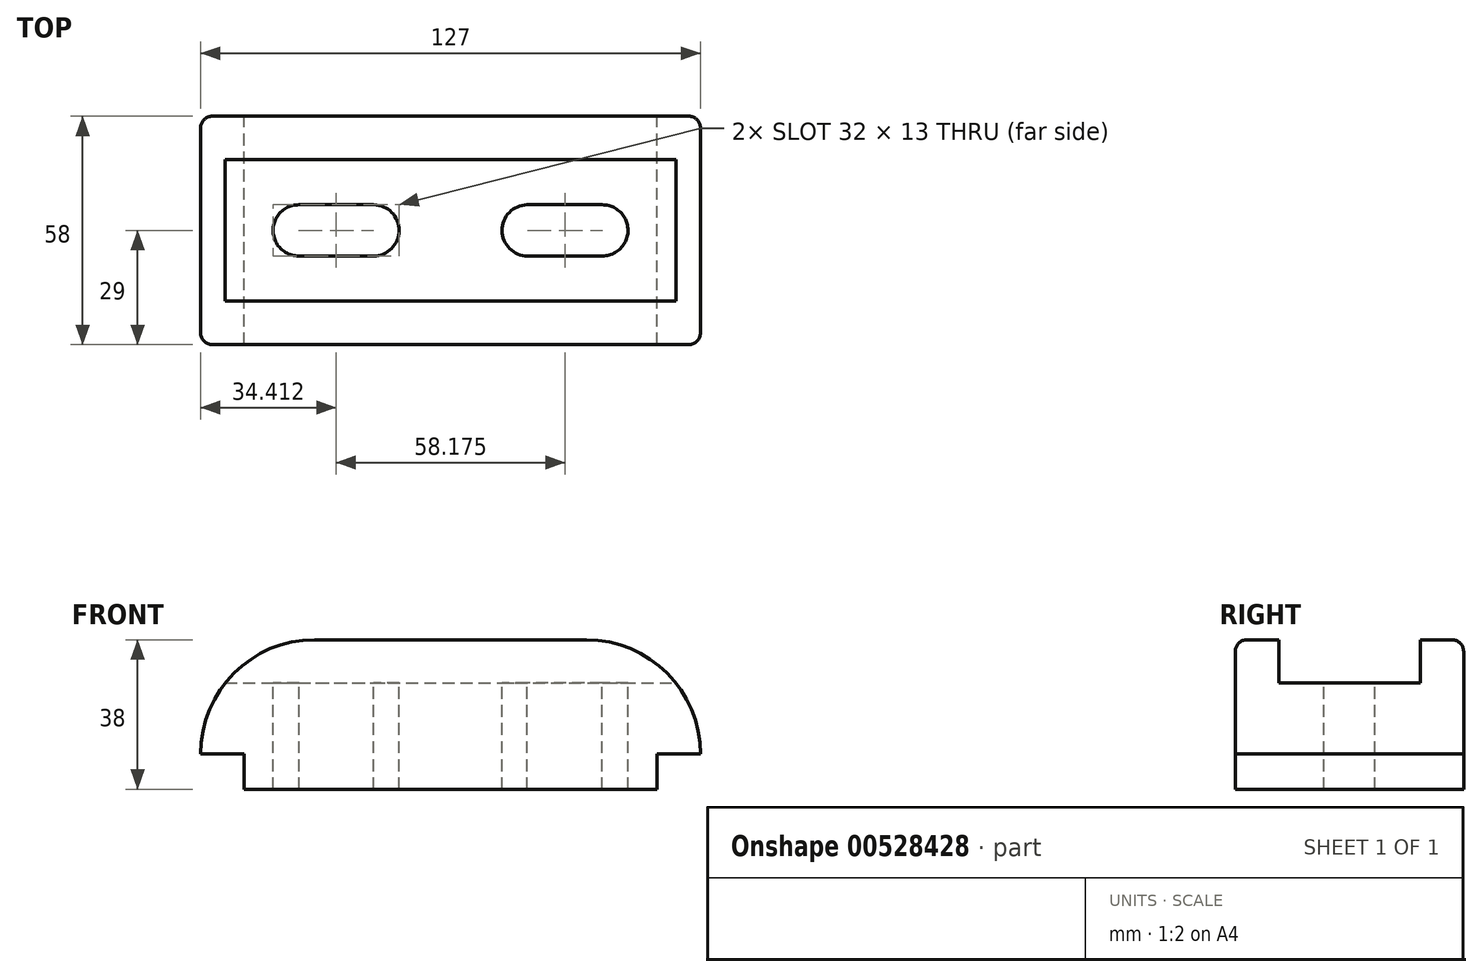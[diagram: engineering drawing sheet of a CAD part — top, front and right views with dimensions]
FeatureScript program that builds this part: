
annotation { "Feature Type Name" : "Feature", "Feature Type Description" : "" }
export const myFeature = defineFeature(function(context is Context, id is Id, definition is map)
    precondition{}
    {
        {
            var Q0;
            Q0=qCreatedBy(makeId("Front.planeOp"),FACE);
            var sketch = newSketch(context, id + "F0", { "sketchPlane" : qUnion([Q0])});
            skLineSegment(sketch, "E0.bottom", {"start": v(-34.5, 19) * mm, "end": v(34.5, 19) * mm});
            skLineSegment(sketch, "E0.top", {"start": v(-52.5, -19) * mm, "end": v(52.5, -19) * mm});
            skLineSegment(sketch, "E0.left", {"start": v(-63.5, -10) * mm, "end": v(-63.5, -10) * mm});
            skLineSegment(sketch, "E0.right", {"start": v(63.5, -10) * mm, "end": v(63.5, -10) * mm});
            skPoint(sketch, "E0.middle", {"position": v(0, 0) * mm});
            skLineSegment(sketch, "E1.bottom", {"start": v(-63.5, -10) * mm, "end": v(-52.5, -10) * mm});
            skLineSegment(sketch, "E1.right", {"start": v(-52.5, -10) * mm, "end": v(-52.5, -19) * mm});
            skPoint(sketch, "E2.orphan", {"position": v(-63.5, -19) * mm});
            skLineSegment(sketch, "E3", {"start": v(0, 19) * mm, "end": v(0, -19) * mm, "construction": true});
            skPoint(sketch, "E4.MirrorP", {"position": v(63.5, -19) * mm});
            skLineSegment(sketch, "E5.MirrorCS", {"start": v(63.5, -10) * mm, "end": v(52.5, -10) * mm});
            skLineSegment(sketch, "E6.MirrorCS", {"start": v(52.5, -10) * mm, "end": v(52.5, -19) * mm});
            skPoint(sketch, "E7.visualSharp", {"position": v(-63.5, 19) * mm});
            skArc(sketch, "E7.filletArc", {"start": v(-34.5, 19) * mm, "mid": v(-55, 10.5) * mm, "end": v(-63.5, -10) * mm});
            skPoint(sketch, "E8.visualSharp", {"position": v(63.5, 19) * mm});
            skArc(sketch, "E8.filletArc", {"start": v(63.5, -10) * mm, "mid": v(55, 10.5) * mm, "end": v(34.5, 19) * mm});
            skSolve(sketch);
        }
        {
            var Q0;
            Q0 = qSketchRegion(id + "F0", true);
            extrude(context, id + "F1", {"entities" : qUnion([Q0]), "depth" : 58 * mm, "offsetDistance" : 25 * mm});
        }
        {
            var Q0;
            Q0=makeQuery(id+"F1.opExtrude","SWEPT_FACE",FACE,{"disambiguationData":[OSD([sQuery(id+"F0.wireOp",EDGE,"E0.bottom")])]});
            var sketch = newSketch(context, id + "F2", { "sketchPlane" : qUnion([Q0])});
            skLineSegment(sketch, "E9.bottom", {"start": v(-85.95, -11) * mm, "end": v(85.95, -11) * mm});
            skLineSegment(sketch, "E9.top", {"start": v(-85.95, -47) * mm, "end": v(85.95, -47) * mm});
            skLineSegment(sketch, "E9.left", {"start": v(-85.95, -11) * mm, "end": v(-85.95, -47) * mm});
            skLineSegment(sketch, "E9.right", {"start": v(85.95, -11) * mm, "end": v(85.95, -47) * mm});
            skPoint(sketch, "E9.middle", {"position": v(0, -29) * mm});
            skPoint(sketch, "E9.middle.positionSnap0", {"position": v(-34.5, -29) * mm});
            skPoint(sketch, "E9.centerSnap0", {"position": v(-34.5, -29) * mm});
            skSolve(sketch);
        }
        {
            var Q0;
            Q0 = qSketchRegion(id + "F2", true);
            extrude(context, id + "F3", {"entities" : qUnion([Q0]), "operationType" : NewBodyOperationType.REMOVE, "oppositeDirection" : true, "depth" : 11 * mm, "offsetDistance" : 25 * mm});
        }
        {
            var Q0;
            Q0=makeQuery(id+"F3.boolean.opBoolean","COPY",FACE,{"derivedFrom":makeQuery(id+"F3.opExtrude","CAP_FACE",FACE,{"disambiguationData":[OSD([sQuery(id+"F2.wireOp",EDGE,"E9.bottom"),sQuery(id+"F2.wireOp",EDGE,"E9.top"),sQuery(id+"F2.wireOp",EDGE,"E9.left"),sQuery(id+"F2.wireOp",EDGE,"E9.right")])],"isStart":false})});
            var sketch = newSketch(context, id + "F4", { "sketchPlane" : qUnion([Q0])});
            skLineSegment(sketch, "E10.bottom", {"start": v(-38.5, -22.5) * mm, "end": v(-19.5, -22.5) * mm});
            skLineSegment(sketch, "E10.top", {"start": v(-38.59, -35.5) * mm, "end": v(-19.59, -35.5) * mm});
            skPoint(sketch, "E10.middle", {"position": v(-29.04, -29) * mm});
            skPoint(sketch, "E10.middle.positionSnap0", {"position": v(-57.24, -29) * mm});
            skPoint(sketch, "E10.centerSnap0", {"position": v(-57.24, -29) * mm});
            skArc(sketch, "E11", {"start": v(-38.5, -22.5) * mm, "mid": v(-45.09, -28.96) * mm, "end": v(-38.59, -35.5) * mm});
            skArc(sketch, "E12", {"start": v(-19.59, -35.5) * mm, "mid": v(-13.09, -29.04) * mm, "end": v(-19.5, -22.5) * mm});
            skLineSegment(sketch, "E13", {"start": v(0, 0) * mm, "end": v(0, -58.22) * mm, "construction": true});
            skLineSegment(sketch, "E14.MirrorCS", {"start": v(38.59, -35.5) * mm, "end": v(19.59, -35.5) * mm});
            skLineSegment(sketch, "E15.MirrorCS", {"start": v(38.5, -22.5) * mm, "end": v(19.5, -22.5) * mm});
            skPoint(sketch, "E16.MirrorP", {"position": v(29.04, -29) * mm});
            skArc(sketch, "E17.MirrorCS", {"start": v(19.59, -35.5) * mm, "mid": v(13.09, -29.04) * mm, "end": v(19.5, -22.5) * mm});
            skArc(sketch, "E18.MirrorCS", {"start": v(38.5, -22.5) * mm, "mid": v(45.09, -28.96) * mm, "end": v(38.59, -35.5) * mm});
            skSolve(sketch);
        }
        {
            var Q0;
            Q0 = qSketchRegion(id + "F4", true);
            extrude(context, id + "F5", {"entities" : qUnion([Q0]), "operationType" : NewBodyOperationType.REMOVE, "endBound" : BoundingType.THROUGH_ALL, "oppositeDirection" : true, "depth" : 25 * mm, "offsetDistance" : 25 * mm});
        }
        {
            var Q0;
            Q0=makeQuery(id+"F1.opExtrude","CAP_EDGE",EDGE,{"disambiguationData":[OSD([sQuery(id+"F0.wireOp",EDGE,"E0.bottom")])],"isStart":false});
            var Q1;
            Q1=makeQuery(id+"F1.opExtrude","CAP_EDGE",EDGE,{"disambiguationData":[OSD([sQuery(id+"F0.wireOp",EDGE,"E0.bottom")])],"isStart":true});
            fillet(context, id + "F6", {"entities" : qUnion([Q0, Q1]), "radius" : 3 * mm, "tangentPropagation" : true, "allowEdgeOverflow" : false});
        }
    });
